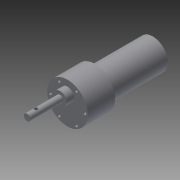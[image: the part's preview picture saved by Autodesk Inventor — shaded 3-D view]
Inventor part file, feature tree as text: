
AUTODESK INVENTOR PART (.ipt)
format: ipt  version: 2015 (Build 190159000, 159)  size: 124,928 bytes
history: native  units: in
note: dims shown in document units (in); Inventor stores cm internally (conversion verified against a paired STEP export)
features: extrude x4, sketch x2, revolve x1
ambient origin geometry x8: Origin, YZ Plane, XZ Plane, XY Plane, X Axis, Y Axis, Z Axis, Center Point
bodies: Solid1 (feature_tree)
feature tree (7):
  sketch  "Sketch1"  dims[d1=0.9843in d2=2.0866in]
  revolve  "Revolution1"  [1 undecoded]
  sketch  "Sketch2"  dims[d4=90.0deg d12=0.1181in d13=0.1181in d14=0.2756in d15=0.4724in d16=0.2362in d17=0.1181in d18=0.1181in d19=0.1181in d20=0.1181in d21=0.2677in d22=0.0in d23=1.4488in d24=0.0in d25=0.1969in d26=0.0in d30=1.4488in d31=0.315in d32=0.1181in d33=0.7874in d34=0.0in]
  extrude  "Extrusion3"  Depth=0.1181in
  extrude  "Extrusion4"  Depth=0.1181in
  extrude  "Extrusion5"  Depth=0.2756in
  extrude  "Extrusion6"  Depth=0.4724in
note: 1 required parameter value undecoded (feature->parameter linkage not recoverable at this tier; creation-order binding heuristic only, values carry confidence <= 0.55)
